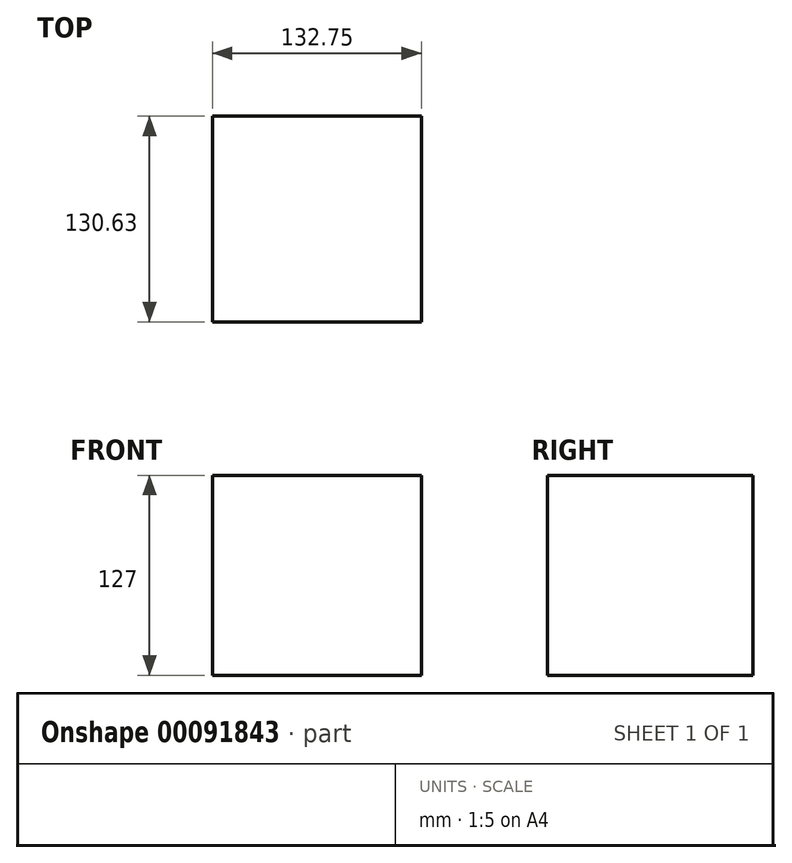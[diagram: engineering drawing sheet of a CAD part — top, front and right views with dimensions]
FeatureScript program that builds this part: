
annotation { "Feature Type Name" : "Feature", "Feature Type Description" : "" }
export const myFeature = defineFeature(function(context is Context, id is Id, definition is map)
    precondition{}
    {
        {
            var Q0;
            Q0=qCreatedBy(makeId("Top.planeOp"),FACE);
            var sketch = newSketch(context, id + "F0", { "sketchPlane" : qUnion([Q0])});
            skLineSegment(sketch, "E0.bottom", {"start": v(0, 0) * mm, "end": v(132.75, 0) * mm});
            skLineSegment(sketch, "E0.top", {"start": v(0, -130.63) * mm, "end": v(132.75, -130.63) * mm});
            skLineSegment(sketch, "E0.left", {"start": v(0, 0) * mm, "end": v(0, -130.63) * mm});
            skLineSegment(sketch, "E0.right", {"start": v(132.75, 0) * mm, "end": v(132.75, -130.63) * mm});
            skSolve(sketch);
        }
        {
            var Q0;
            Q0=makeQuery(id+"F0.imprint","IMPRINT",FACE,{"disambiguationData":[TD([[makeQuery(id+"F0.imprint","IMPRINT",EDGE,{"derivedFrom":sQuery(id+"F0.wireOp",EDGE,"E0.bottom")}),-1.0]])]});
            extrude(context, id + "F1", {"entities" : qUnion([Q0]), "depth" : 127 * mm});
        }
    });
